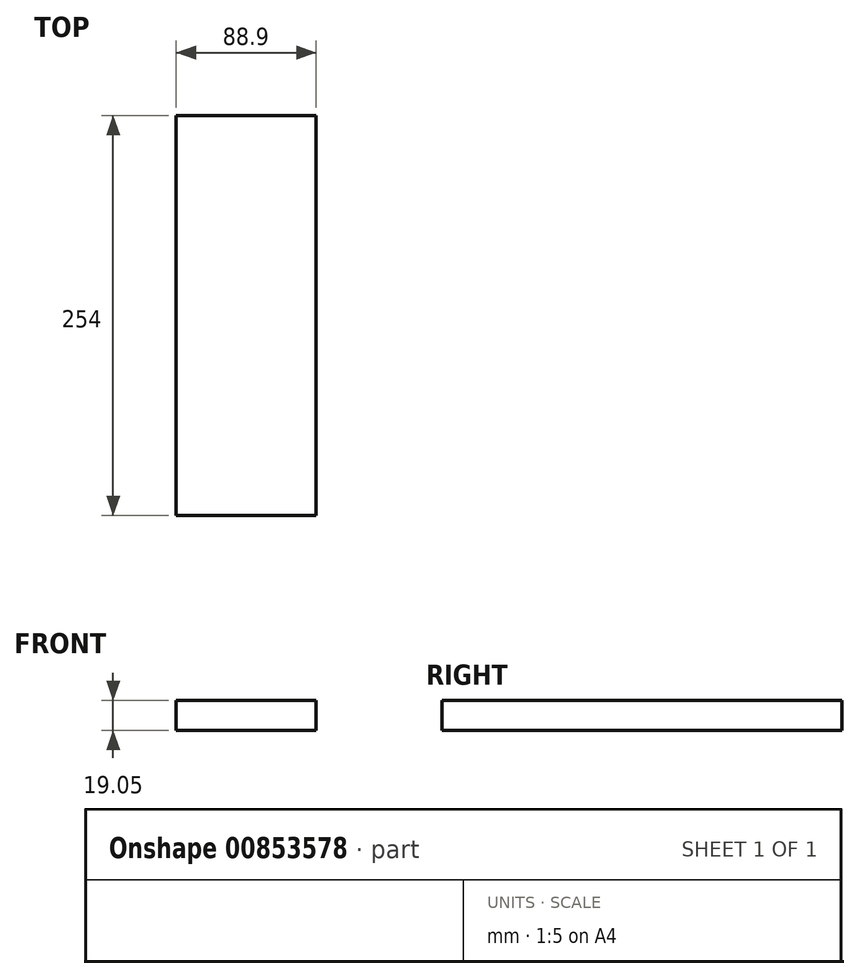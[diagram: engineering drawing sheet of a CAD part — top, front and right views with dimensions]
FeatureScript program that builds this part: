
annotation { "Feature Type Name" : "Feature", "Feature Type Description" : "" }
export const myFeature = defineFeature(function(context is Context, id is Id, definition is map)
    precondition{}
    {
        {
            var Q0;
            Q0=qCreatedBy(makeId("Front.planeOp"),FACE);
            var sketch = newSketch(context, id + "F0", { "sketchPlane" : qUnion([Q0])});
            skLineSegment(sketch, "E0.bottom", {"start": v(0, 0) * mm, "end": v(88.9, 0) * mm});
            skLineSegment(sketch, "E0.top", {"start": v(0, 19.05) * mm, "end": v(88.9, 19.05) * mm});
            skLineSegment(sketch, "E0.left", {"start": v(0, 0) * mm, "end": v(0, 19.05) * mm});
            skLineSegment(sketch, "E0.right", {"start": v(88.9, 0) * mm, "end": v(88.9, 19.05) * mm});
            skSolve(sketch);
        }
        {
            var Q0;
            Q0=makeQuery(id+"F0.imprint","IMPRINT",FACE,{"disambiguationData":[TD([[makeQuery(id+"F0.imprint","IMPRINT",EDGE,{"derivedFrom":sQuery(id+"F0.wireOp",EDGE,"E0.bottom")}),1.0]])]});
            extrude(context, id + "F1", {"entities" : qUnion([Q0]), "depth" : 254 * mm, "offsetDistance" : 25.4 * mm});
        }
    });
